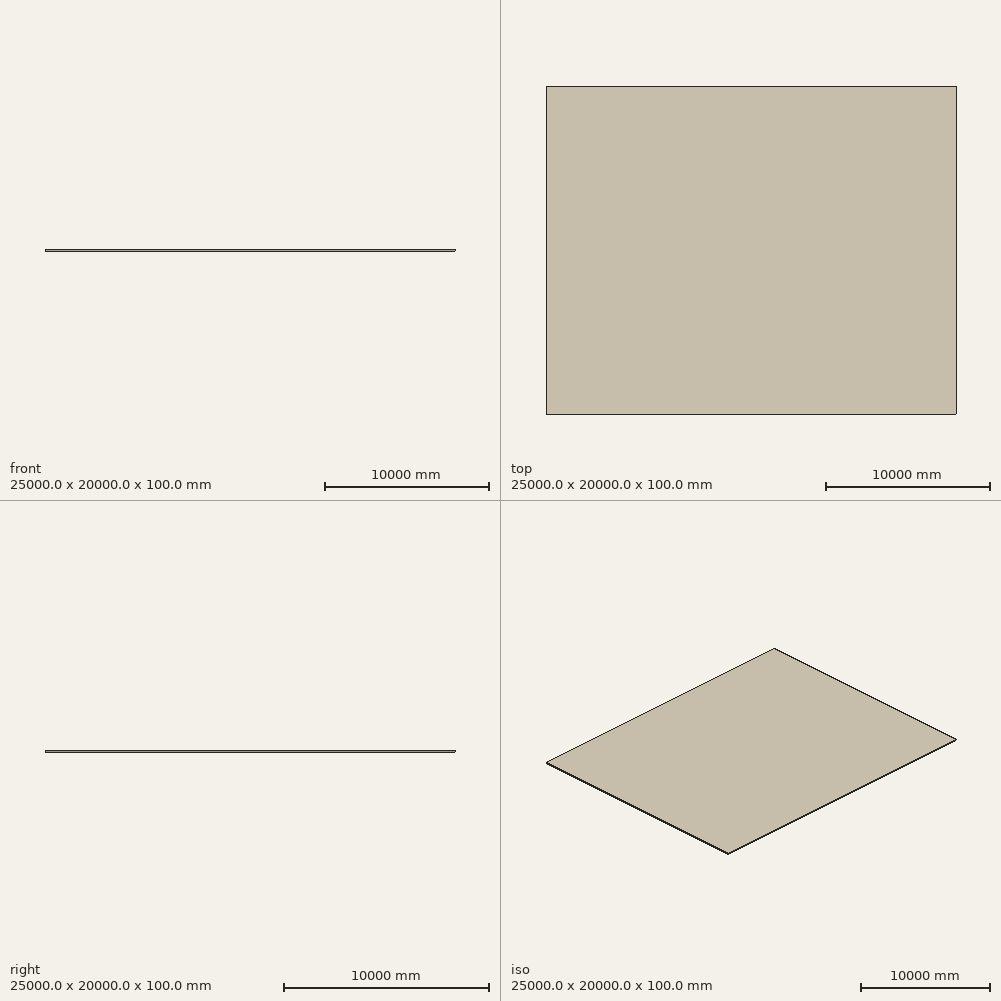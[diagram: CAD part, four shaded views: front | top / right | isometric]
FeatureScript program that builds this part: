
annotation { "Feature Type Name" : "Feature", "Feature Type Description" : "" }
export const myFeature = defineFeature(function(context is Context, id is Id, definition is map)
    precondition{}
    {
        {
            var Q0;
            Q0=qCreatedBy(makeId("Top.planeOp"),FACE);
            var sketch = newSketch(context, id + "F0", { "sketchPlane" : qUnion([Q0])});
            skLineSegment(sketch, "E0.bottom", {"start": v(-12500, 10000) * mm, "end": v(12500, 10000) * mm});
            skLineSegment(sketch, "E0.top", {"start": v(-12500, -10000) * mm, "end": v(12500, -10000) * mm});
            skLineSegment(sketch, "E0.left", {"start": v(-12500, 10000) * mm, "end": v(-12500, -10000) * mm});
            skLineSegment(sketch, "E0.right", {"start": v(12500, 10000) * mm, "end": v(12500, -10000) * mm});
            skPoint(sketch, "E0.middle", {"position": v(0, 0) * mm});
            skSolve(sketch);
        }
        {
            var Q0;
            Q0=makeQuery(id+"F0.imprint","IMPRINT",FACE,{"disambiguationData":[TD([[makeQuery(id+"F0.imprint","IMPRINT",EDGE,{"derivedFrom":sQuery(id+"F0.wireOp",EDGE,"E0.bottom")}),-1.0]])]});
            extrude(context, id + "F1", {"entities" : qUnion([Q0]), "oppositeDirection" : true, "depth" : 100 * mm, "offsetDistance" : 25 * mm});
        }
    });
